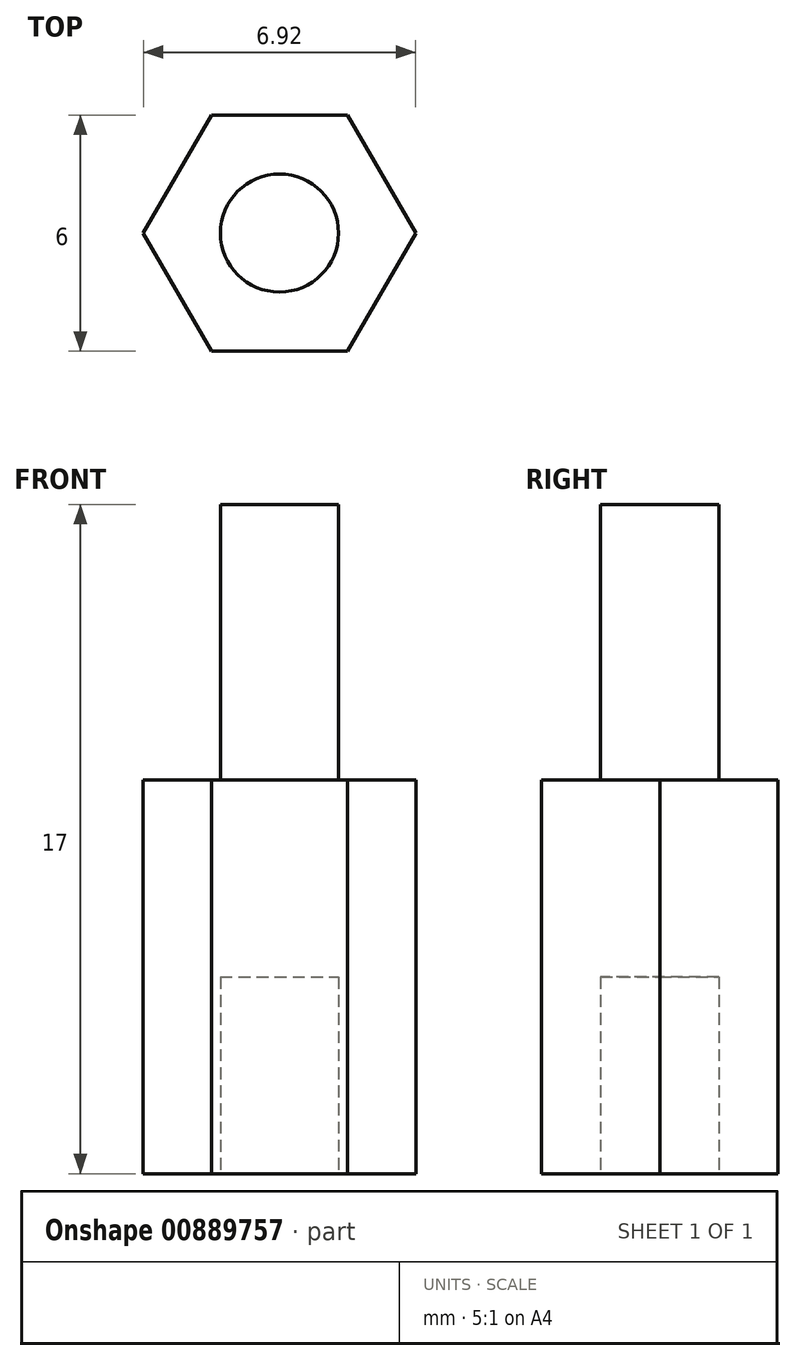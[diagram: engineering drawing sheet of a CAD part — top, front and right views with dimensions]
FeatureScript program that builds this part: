
annotation { "Feature Type Name" : "Feature", "Feature Type Description" : "" }
export const myFeature = defineFeature(function(context is Context, id is Id, definition is map)
    precondition{}
    {
        {
            var Q0;
            Q0=qCreatedBy(makeId("Top.planeOp"),FACE);
            var sketch = newSketch(context, id + "F0", { "sketchPlane" : qUnion([Q0])});
            skCircle(sketch, "E0.cCircle", {"center": v(0, 0) * mm, "radius": 3 * mm, "construction": true});
            skLineSegment(sketch, "E0.0", {"start": v(-1.73, 3) * mm, "end": v(1.73, 3) * mm});
            skLineSegment(sketch, "E0.1", {"start": v(1.73, 3) * mm, "end": v(3.46, 0) * mm});
            skLineSegment(sketch, "E0.2", {"start": v(3.46, 0) * mm, "end": v(1.73, -3) * mm});
            skLineSegment(sketch, "E0.3", {"start": v(1.73, -3) * mm, "end": v(-1.73, -3) * mm});
            skLineSegment(sketch, "E0.4", {"start": v(-1.73, -3) * mm, "end": v(-3.46, 0) * mm});
            skLineSegment(sketch, "E0.5", {"start": v(-3.46, 0) * mm, "end": v(-1.73, 3) * mm});
            skPoint(sketch, "E0.0.midPoint", {"position": v(0, 3) * mm});
            skSolve(sketch);
        }
        {
            var Q0;
            Q0=makeQuery(id+"F0.imprint","IMPRINT",FACE,{"disambiguationData":[TD([[makeQuery(id+"F0.imprint","IMPRINT",EDGE,{"derivedFrom":sQuery(id+"F0.wireOp",EDGE,"E0.0")}),-1.0]])]});
            extrude(context, id + "F1", {"entities" : qUnion([Q0]), "depth" : 10 * mm});
        }
        {
            var Q0;
            Q0=makeQuery(id+"F1.opExtrude","CAP_FACE",FACE,{"disambiguationData":[OSD([sQuery(id+"F0.wireOp",EDGE,"E0.0"),sQuery(id+"F0.wireOp",EDGE,"E0.1"),sQuery(id+"F0.wireOp",EDGE,"E0.2"),sQuery(id+"F0.wireOp",EDGE,"E0.3"),sQuery(id+"F0.wireOp",EDGE,"E0.4"),sQuery(id+"F0.wireOp",EDGE,"E0.5")])],"isStart":false});
            var sketch = newSketch(context, id + "F2", { "sketchPlane" : qUnion([Q0])});
            skLineSegment(sketch, "E1", {"start": v(-1.73, 3) * mm, "end": v(1.73, -3) * mm, "construction": true});
            skCircle(sketch, "E2", {"center": v(0, 0) * mm, "radius": 1.5 * mm});
            skSolve(sketch);
        }
        {
            var Q0;
            Q0=makeQuery(id+"F2.imprint","IMPRINT",FACE,{"disambiguationData":[TD([[makeQuery(id+"F2.imprint","IMPRINT",EDGE,{"derivedFrom":sQuery(id+"F2.wireOp",EDGE,"E2")}),1.0]])]});
            extrude(context, id + "F3", {"entities" : qUnion([Q0]), "operationType" : NewBodyOperationType.ADD, "depth" : 7 * mm});
        }
        {
            var Q0;
            Q0=makeQuery(id+"F1.opExtrude","CAP_FACE",FACE,{"disambiguationData":[OSD([sQuery(id+"F0.wireOp",EDGE,"E0.0"),sQuery(id+"F0.wireOp",EDGE,"E0.1"),sQuery(id+"F0.wireOp",EDGE,"E0.2"),sQuery(id+"F0.wireOp",EDGE,"E0.3"),sQuery(id+"F0.wireOp",EDGE,"E0.4"),sQuery(id+"F0.wireOp",EDGE,"E0.5")])],"isStart":true});
            var sketch = newSketch(context, id + "F4", { "sketchPlane" : qUnion([Q0])});
            skLineSegment(sketch, "E3", {"start": v(1.73, -3) * mm, "end": v(-1.73, 3) * mm, "construction": true});
            skCircle(sketch, "E4", {"center": v(0, 0) * mm, "radius": 1.5 * mm});
            skSolve(sketch);
        }
        {
            var Q0;
            Q0=qSketchRegion(id+"F4",true);
            extrude(context, id + "F5", {"entities" : qUnion([Q0]), "operationType" : NewBodyOperationType.REMOVE, "oppositeDirection" : true, "depth" : 5 * mm});
        }
    });
